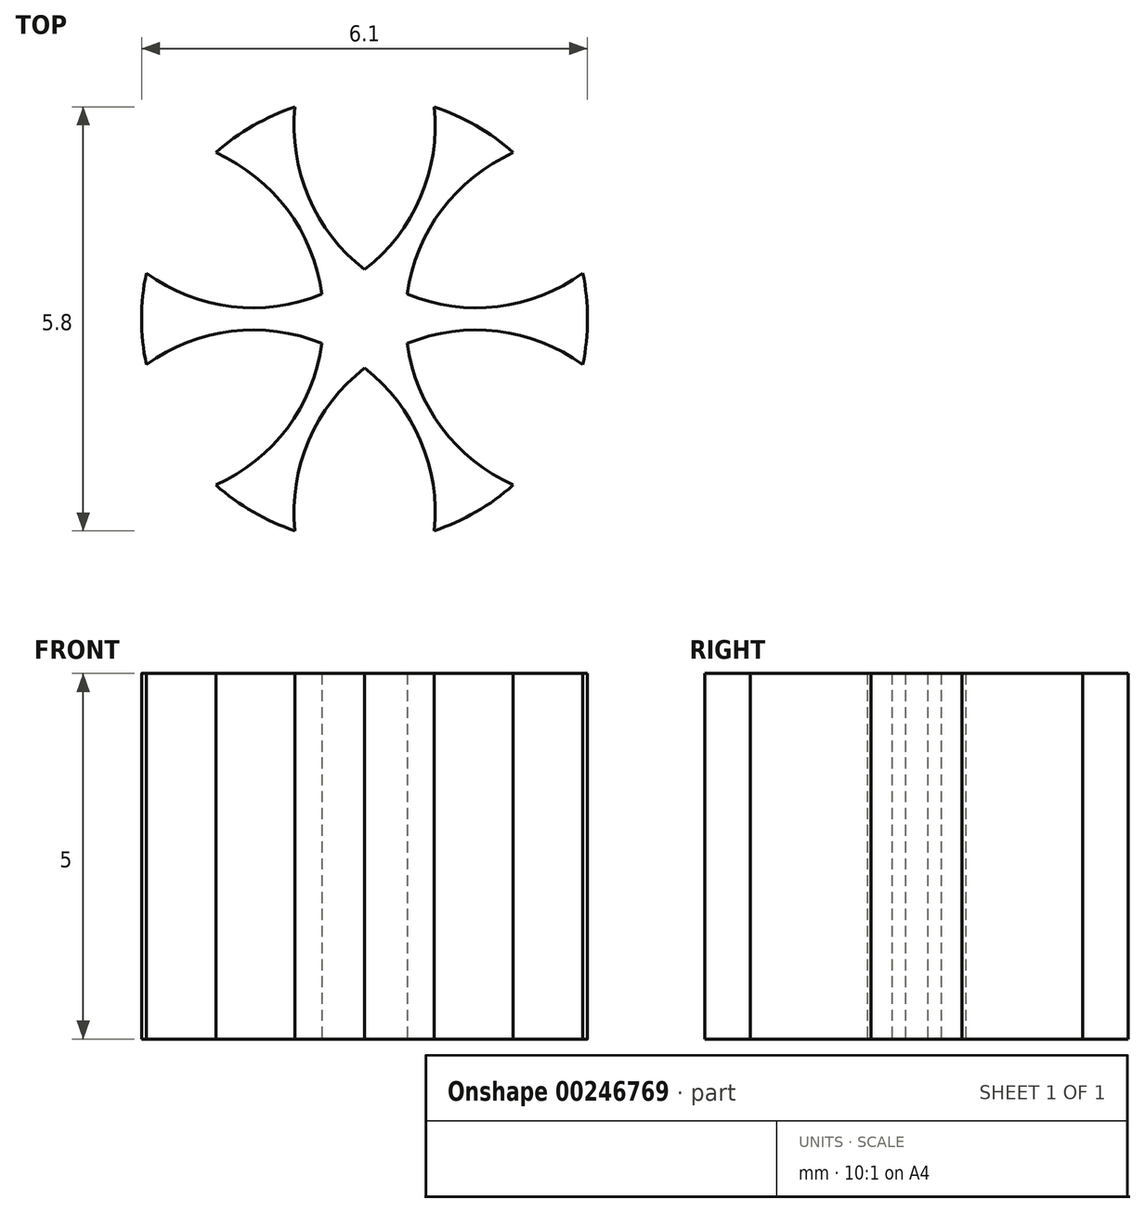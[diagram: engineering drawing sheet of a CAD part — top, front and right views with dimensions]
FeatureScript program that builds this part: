
annotation { "Feature Type Name" : "Feature", "Feature Type Description" : "" }
export const myFeature = defineFeature(function(context is Context, id is Id, definition is map)
    precondition{}
    {
        {
            var Q0;
            Q0=qCreatedBy(makeId("Top.planeOp"),FACE);
            var sketch = newSketch(context, id + "F0", { "sketchPlane" : qUnion([Q0])});
            skCircle(sketch, "E0", {"center": v(0, 0) * mm, "radius": 3.05 * mm});
            skArc(sketch, "E1.cCircle", {"start": v(-3, 0.52) * mm, "mid": v(1.53, -2.64) * mm, "end": v(1.04, 2.87) * mm, "construction": true});
            skPoint(sketch, "E2.orphan", {"position": v(3.05, 0) * mm});
            skCircle(sketch, "E3", {"center": v(3.05, 0) * mm, "radius": 2.5 * mm});
            skCircle(sketch, "E4.1.0", {"center": v(1.53, 2.64) * mm, "radius": 2.5 * mm});
            skCircle(sketch, "E4.2.0", {"center": v(-1.52, 2.64) * mm, "radius": 2.5 * mm});
            skCircle(sketch, "E4.3.0", {"center": v(-3.05, 0) * mm, "radius": 2.5 * mm});
            skCircle(sketch, "E4.4.0", {"center": v(-1.53, -2.64) * mm, "radius": 2.5 * mm});
            skCircle(sketch, "E4.5.0", {"center": v(1.53, -2.64) * mm, "radius": 2.5 * mm});
            skSolve(sketch);
        }
        {
            var Q0;
            {var subQ0=sQuery(id+"F0.wireOp",EDGE,"E4.1.0");var subQ1=sQuery(id+"F0.wireOp",EDGE,"E0");var subQ2=makeQuery(id+"F0.imprint","INTERSECT",VERTEX,{"disambiguationData":[OD(1.0)],"derivedFrom":[subQ1,subQ0]});Q0=makeQuery(id+"F0.imprint","IMPRINT",FACE,{"disambiguationData":[TD([[makeQuery(id+"F0.imprint","IMPRINT",EDGE,{"disambiguationData":[TD([[subQ2,-1.0]])],"derivedFrom":subQ1}),1.0]])]});}
            var Q1;
            {var subQ0=sQuery(id+"F0.wireOp",EDGE,"E4.2.0");var subQ1=sQuery(id+"F0.wireOp",EDGE,"E0");var subQ2=makeQuery(id+"F0.imprint","INTERSECT",VERTEX,{"disambiguationData":[OD(1.0)],"derivedFrom":[subQ1,subQ0]});Q1=makeQuery(id+"F0.imprint","IMPRINT",FACE,{"disambiguationData":[TD([[makeQuery(id+"F0.imprint","IMPRINT",EDGE,{"disambiguationData":[TD([[subQ2,-1.0]])],"derivedFrom":subQ1}),1.0]])]});}
            var Q2;
            {var subQ5=sQuery(id+"F0.wireOp",EDGE,"E4.1.0");var subQ7=sQuery(id+"F0.wireOp",EDGE,"E3");var subQ8=makeQuery(id+"F0.imprint","INTERSECT",VERTEX,{"disambiguationData":[OD(1.0)],"derivedFrom":[subQ7,subQ5]});Q2=makeQuery(id+"F0.imprint","IMPRINT",FACE,{"disambiguationData":[TD([[makeQuery(id+"F0.imprint","IMPRINT",EDGE,{"disambiguationData":[TD([[subQ8,-1.0]])],"derivedFrom":subQ7}),-1.0]])]});}
            var Q3;
            {var subQ0=sQuery(id+"F0.wireOp",EDGE,"E3");var subQ1=sQuery(id+"F0.wireOp",EDGE,"E0");var subQ2=makeQuery(id+"F0.imprint","INTERSECT",VERTEX,{"disambiguationData":[OD(0.0)],"derivedFrom":[subQ1,subQ0]});Q3=makeQuery(id+"F0.imprint","IMPRINT",FACE,{"disambiguationData":[TD([[makeQuery(id+"F0.imprint","IMPRINT",EDGE,{"disambiguationData":[TD([[subQ2,-1.0]])],"derivedFrom":subQ1}),1.0]])]});}
            var Q4;
            {var subQ0=sQuery(id+"F0.wireOp",EDGE,"E4.1.0");var subQ1=sQuery(id+"F0.wireOp",EDGE,"E0");var subQ2=makeQuery(id+"F0.imprint","INTERSECT",VERTEX,{"disambiguationData":[OD(0.0)],"derivedFrom":[subQ1,subQ0]});Q4=makeQuery(id+"F0.imprint","IMPRINT",FACE,{"disambiguationData":[TD([[makeQuery(id+"F0.imprint","IMPRINT",EDGE,{"disambiguationData":[TD([[subQ2,1.0]])],"derivedFrom":subQ1}),1.0]])]});}
            var Q5;
            {var subQ0=sQuery(id+"F0.wireOp",EDGE,"E4.4.0");var subQ1=sQuery(id+"F0.wireOp",EDGE,"E0");var subQ2=makeQuery(id+"F0.imprint","INTERSECT",VERTEX,{"disambiguationData":[OD(1.0)],"derivedFrom":[subQ1,subQ0]});Q5=makeQuery(id+"F0.imprint","IMPRINT",FACE,{"disambiguationData":[TD([[makeQuery(id+"F0.imprint","IMPRINT",EDGE,{"disambiguationData":[TD([[subQ2,-1.0]])],"derivedFrom":subQ1}),1.0]])]});}
            var Q6;
            {var subQ0=sQuery(id+"F0.wireOp",EDGE,"E4.3.0");var subQ1=sQuery(id+"F0.wireOp",EDGE,"E0");var subQ2=makeQuery(id+"F0.imprint","INTERSECT",VERTEX,{"disambiguationData":[OD(1.0)],"derivedFrom":[subQ1,subQ0]});Q6=makeQuery(id+"F0.imprint","IMPRINT",FACE,{"disambiguationData":[TD([[makeQuery(id+"F0.imprint","IMPRINT",EDGE,{"disambiguationData":[TD([[subQ2,-1.0]])],"derivedFrom":subQ1}),1.0]])]});}
            extrude(context, id + "F1", {"entities" : qUnion([Q0, Q1, Q2, Q3, Q4, Q5, Q6]), "depth" : 5 * mm});
        }
    });
